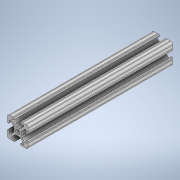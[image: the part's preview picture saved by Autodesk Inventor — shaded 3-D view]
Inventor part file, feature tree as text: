
AUTODESK INVENTOR PART (.ipt)
format: ipt  version: 2020 (Build 240168000, 168)  size: 236,032 bytes
history: native  units: in
note: dims shown in document units (in); Inventor stores cm internally (conversion verified against a paired STEP export)
features: extrude x1, sketch x1
ambient origin geometry x8: Origin, YZ Plane, XZ Plane, XY Plane, X Axis, Y Axis, Z Axis, Center Point
bodies: Solid1 (feature_tree)
feature tree (2):
  extrude  "Extrusion1"  [1 undecoded]
  sketch  "Sketch1"  dims[d0=7.0in d1=0.0in]
note: 1 required parameter value undecoded (feature->parameter linkage not recoverable at this tier; creation-order binding heuristic only, values carry confidence <= 0.55)
